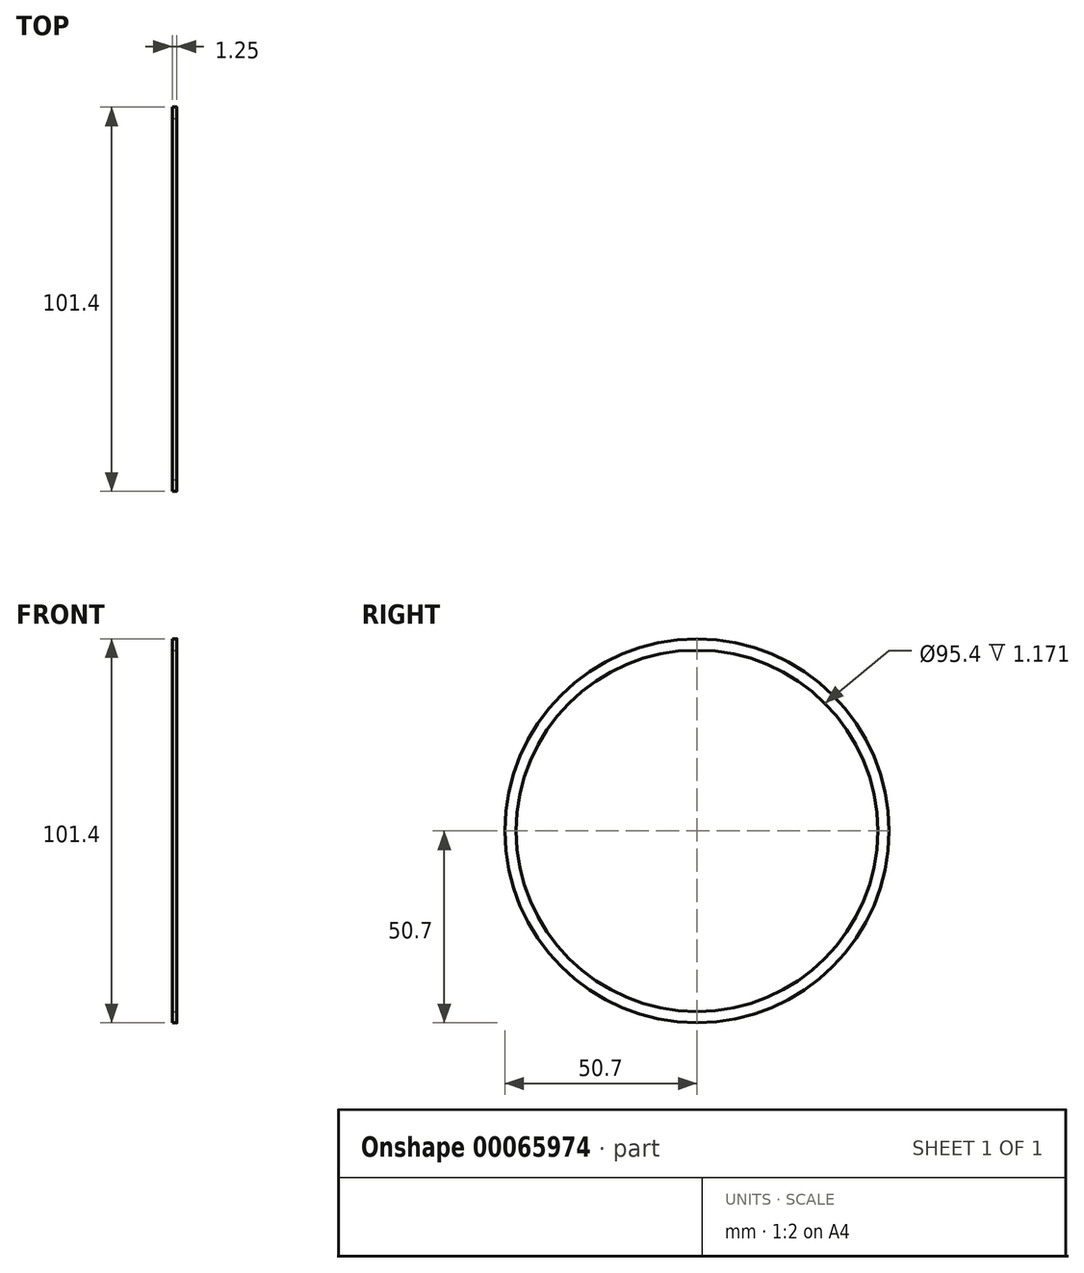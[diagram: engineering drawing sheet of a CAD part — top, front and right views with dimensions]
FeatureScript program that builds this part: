
annotation { "Feature Type Name" : "Feature", "Feature Type Description" : "" }
export const myFeature = defineFeature(function(context is Context, id is Id, definition is map)
    precondition{}
    {
        {
            var Q0;
            Q0=qCreatedBy(makeId("Front.planeOp"),FACE);
            var sketch = newSketch(context, id + "F0", { "sketchPlane" : qUnion([Q0])});
            skLineSegment(sketch, "E0.bottom", {"start": v(-0.1, 50.7) * mm, "end": v(-1.28, 50.7) * mm});
            skLineSegment(sketch, "E0.top", {"start": v(-0.1, 47.7) * mm, "end": v(-1.28, 47.7) * mm});
            skLineSegment(sketch, "E0.right", {"start": v(-1.28, 50.7) * mm, "end": v(-1.28, 47.7) * mm});
            skLineSegment(sketch, "E1", {"start": v(0, 0) * mm, "end": v(-6.16, 0) * mm, "construction": true});
            skArc(sketch, "E2", {"start": v(-0.03, 50.6) * mm, "mid": v(-0.26, 49.2) * mm, "end": v(-0.03, 47.8) * mm});
            skPoint(sketch, "E3.visualSharp", {"position": v(0, 50.7) * mm});
            skArc(sketch, "E3.filletArc", {"start": v(-0.03, 50.6) * mm, "mid": v(-0.05, 50.67) * mm, "end": v(-0.1, 50.7) * mm});
            skPoint(sketch, "E4.visualSharp", {"position": v(0, 47.7) * mm});
            skArc(sketch, "E4.filletArc", {"start": v(-0.1, 47.7) * mm, "mid": v(-0.05, 47.73) * mm, "end": v(-0.03, 47.8) * mm});
            skLineSegment(sketch, "E5", {"start": v(0, 47.7) * mm, "end": v(0, 0) * mm, "construction": true});
            skSolve(sketch);
        }
        {
            var Q0;
            Q0=makeQuery(id+"F0.imprint","IMPRINT",FACE,{"disambiguationData":[TD([[makeQuery(id+"F0.imprint","IMPRINT",EDGE,{"derivedFrom":sQuery(id+"F0.wireOp",EDGE,"E0.bottom")}),1.0]])]});
            var Q1;
            Q1=sQuery(id+"F0.wireOp",EDGE,"E1");
            revolve(context, id + "F1", {"entities" : qUnion([Q0]), "axis" : qUnion([Q1]), "revolveType" : RevolveType.FULL});
        }
    });
